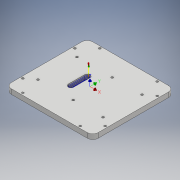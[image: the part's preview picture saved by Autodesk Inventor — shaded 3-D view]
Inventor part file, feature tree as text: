
AUTODESK INVENTOR PART (.ipt)
format: ipt  version: 2017 (Build 210142000, 142)  size: 300,032 bytes
history: native  units: mm
features: extrude x1, sketch x1
ambient origin geometry x8: Origin, YZ Plane, XZ Plane, XY Plane, X Axis, Y Axis, Z Axis, Center Point
bodies: Solido1 (feature_tree)
feature tree (2):
  extrude  "Estrusione1"  Depth=9.0mm TaperAngle=0.0deg
  sketch  "Schizzo1"
